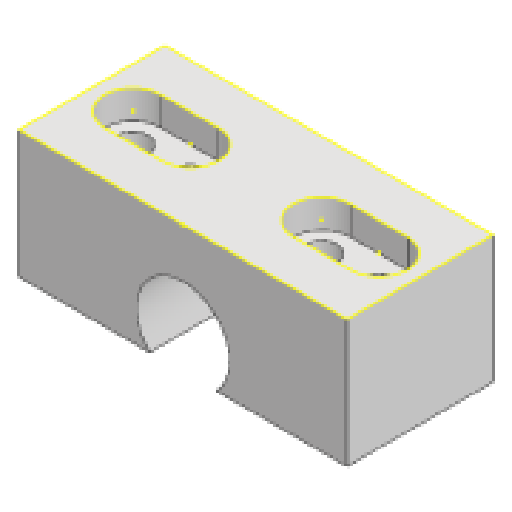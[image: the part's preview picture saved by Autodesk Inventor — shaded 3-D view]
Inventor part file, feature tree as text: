
AUTODESK INVENTOR PART (.ipt)
format: ipt  version: 2025 (Build 290162000, 162)  size: 284,160 bytes
history: native  units: in
note: dims shown in document units (in); Inventor stores cm internally (conversion verified against a paired STEP export)
features: projected_geometry x10, extrude x7, sketch x7, fillet x5, plane x1, mirror x1
ambient origin geometry x8: Origin, YZ Plane, XZ Plane, XY Plane, X Axis, Y Axis, Z Axis, Center Point
bodies: Solid1 (feature_tree)
feature tree (31):
  extrude  "Extrusion1"  Depth=0.458in
  extrude  "Extrusion2"  Depth=0.875in
  plane  "Work Plane1"
  extrude  "Extrusion3"  Depth=1.0in TaperAngle=0.0deg
  mirror  "Mirror1"
  extrude  "Extrusion4"  Depth=0.2165in
  extrude  "Extrusion5"  TaperAngle=0.0deg  [1 undecoded]
  extrude  "Extrusion6"  Depth=3.0in
  fillet  "Fillet2"  Radius=1.0in
  fillet  "Fillet3"  Radius=1.0in
  fillet  "Fillet4"  Radius=0.315in
  extrude  "Extrusion7"  Depth=5.0in
  fillet  "Fillet5"  Radius=1.0in
  fillet  "Fillet6"  Radius=0.25in
  sketch  "Sketch1"  dims[d0=0.635in d1=0.458in]
  sketch  "Sketch2"  dims[d2=2.25in d3=0.875in]
  projected_geometry  "Projected Loop1"
  projected_geometry  "Projected Loop2"
  sketch  "Sketch3"  dims[d4=0.875in d5=1.0in d6=0.0in]
  projected_geometry  "Projected Loop3"
  sketch  "Sketch4"  dims[d7=0.2165in d8=0.2165in]
  projected_geometry  "Projected Loop4"
  sketch  "Sketch5"  dims[d9=0.3937in d10=0.0in d11=0.0in]
  projected_geometry  "Projected Loop5"
  sketch  "Sketch6"  dims[d12=0.315in d13=0.0in d15=3.0in d16=1.0in d17=1.0in d18=0.0in d19=0.315in d20=0.0in]
  projected_geometry  "Projected Loop6"
  projected_geometry  "Projected Loop7"
  projected_geometry  "Projected Loop8"
  sketch  "Sketch7"  dims[d21=0.315in d22=0.0in d23=0.5in d24=1.0in d25=0.25in d26=0.0in d27=0.0in d28=0.25in d29=5.0in]
  projected_geometry  "Projected Loop9"
  projected_geometry  "Projected Loop10"
note: 1 required parameter value undecoded (feature->parameter linkage not recoverable at this tier; creation-order binding heuristic only, values carry confidence <= 0.55)
